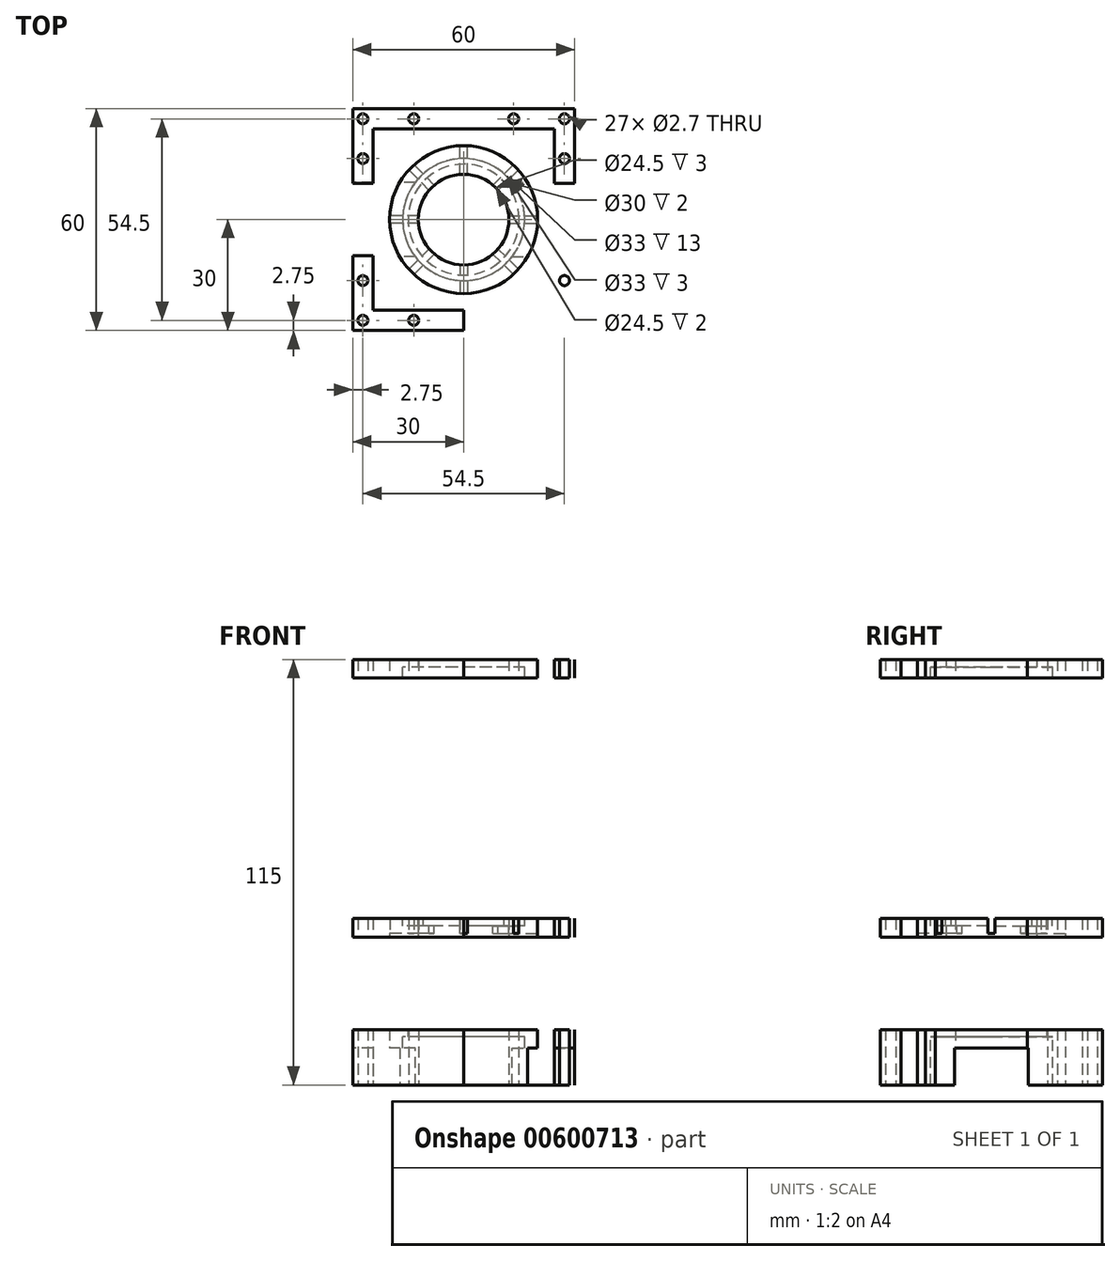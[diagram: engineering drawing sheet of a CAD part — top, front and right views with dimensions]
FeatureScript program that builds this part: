
annotation { "Feature Type Name" : "Feature", "Feature Type Description" : "" }
export const myFeature = defineFeature(function(context is Context, id is Id, definition is map)
    precondition{}
    {
        {
            var Q0;
            Q0=qCreatedBy(makeId("Top.planeOp"),FACE);
            var sketch = newSketch(context, id + "F0", { "sketchPlane" : qUnion([Q0])});
            skLineSegment(sketch, "E0.bottom", {"start": v(12.25, 0) * mm, "end": v(24.5, 0) * mm});
            skLineSegment(sketch, "E0.top", {"start": v(0, 24.5) * mm, "end": v(24.5, 24.5) * mm});
            skLineSegment(sketch, "E0.left", {"start": v(0, 12.25) * mm, "end": v(0, 24.5) * mm});
            skLineSegment(sketch, "E0.right", {"start": v(24.5, 0) * mm, "end": v(24.5, 24.5) * mm});
            skLineSegment(sketch, "E1", {"start": v(0, 24.5) * mm, "end": v(0, 30) * mm});
            skLineSegment(sketch, "E2", {"start": v(0, 30) * mm, "end": v(30, 30) * mm});
            skLineSegment(sketch, "E3", {"start": v(30, 30) * mm, "end": v(30, 9.75) * mm});
            skLineSegment(sketch, "E4", {"start": v(30, 9.75) * mm, "end": v(24.5, 9.75) * mm});
            skCircle(sketch, "E5", {"center": v(0, 0) * mm, "radius": 12.25 * mm});
            skLineSegment(sketch, "E6", {"start": v(0, 27.25) * mm, "end": v(38.5, 27.25) * mm, "construction": true});
            skLineSegment(sketch, "E7", {"start": v(27.25, 9.75) * mm, "end": v(27.25, 36.61) * mm, "construction": true});
            skCircle(sketch, "E8", {"center": v(27.25, 27.25) * mm, "radius": 1.35 * mm});
            skCircle(sketch, "E9", {"center": v(27.25, 16.5) * mm, "radius": 1.35 * mm});
            skCircle(sketch, "E10", {"center": v(13.5, 27.25) * mm, "radius": 1.35 * mm});
            skLineSegment(sketch, "E11.MirrorCS", {"start": v(-30, 30) * mm, "end": v(-30, 9.75) * mm});
            skLineSegment(sketch, "E12.MirrorCS", {"start": v(-24.5, 0) * mm, "end": v(-24.5, 24.5) * mm});
            skLineSegment(sketch, "E13.MirrorCS", {"start": v(-30, 9.75) * mm, "end": v(-24.5, 9.75) * mm});
            skCircle(sketch, "E14.MirrorC", {"center": v(-27.25, 16.5) * mm, "radius": 1.35 * mm});
            skCircle(sketch, "E15.MirrorC", {"center": v(-27.25, 27.25) * mm, "radius": 1.35 * mm});
            skCircle(sketch, "E16.MirrorC", {"center": v(-13.5, 27.25) * mm, "radius": 1.35 * mm});
            skLineSegment(sketch, "E17.MirrorCS", {"start": v(0, 30) * mm, "end": v(-30, 30) * mm});
            skLineSegment(sketch, "E18.MirrorCS", {"start": v(0, 24.5) * mm, "end": v(-24.5, 24.5) * mm});
            skLineSegment(sketch, "E19.MirrorCS", {"start": v(-30, -9.75) * mm, "end": v(-24.5, -9.75) * mm});
            skCircle(sketch, "E20.MirrorC", {"center": v(-27.25, -27.25) * mm, "radius": 1.35 * mm});
            skLineSegment(sketch, "E21.MirrorCS", {"start": v(0, -30) * mm, "end": v(-30, -30) * mm});
            skLineSegment(sketch, "E22.MirrorCS", {"start": v(0, -24.5) * mm, "end": v(-24.5, -24.5) * mm});
            skCircle(sketch, "E23.MirrorC", {"center": v(27.25, -16.5) * mm, "radius": 1.35 * mm});
            skCircle(sketch, "E24.MirrorC", {"center": v(-13.5, -27.25) * mm, "radius": 1.35 * mm});
            skCircle(sketch, "E25.MirrorC", {"center": v(27.25, -27.25) * mm, "radius": 1.35 * mm});
            skLineSegment(sketch, "E26.MirrorCS", {"start": v(30, -9.75) * mm, "end": v(24.5, -9.75) * mm});
            skCircle(sketch, "E27.MirrorC", {"center": v(-27.25, -16.5) * mm, "radius": 1.35 * mm});
            skCircle(sketch, "E28.MirrorC", {"center": v(13.5, -27.25) * mm, "radius": 1.35 * mm});
            skLineSegment(sketch, "E29.MirrorCS", {"start": v(-30, -30) * mm, "end": v(-30, -9.75) * mm});
            skLineSegment(sketch, "E30.MirrorCS", {"start": v(-24.5, 0) * mm, "end": v(-24.5, -24.5) * mm});
            skLineSegment(sketch, "E31.MirrorCS", {"start": v(30, -30) * mm, "end": v(30, -9.75) * mm});
            skLineSegment(sketch, "E32.MirrorCS", {"start": v(0, -30) * mm, "end": v(30, -30) * mm});
            skLineSegment(sketch, "E33.MirrorCS", {"start": v(0, -24.5) * mm, "end": v(24.5, -24.5) * mm});
            skLineSegment(sketch, "E34.MirrorCS", {"start": v(0, -24.5) * mm, "end": v(0, -30) * mm});
            skLineSegment(sketch, "E35.MirrorCS", {"start": v(24.5, 0) * mm, "end": v(24.5, -24.5) * mm});
            skCircle(sketch, "E36", {"center": v(0, 0) * mm, "radius": 20 * mm});
            skSolve(sketch);
        }
        {
            var Q0;
            Q0=qCreatedBy(makeId("Top.planeOp"),FACE);
            var sketch = newSketch(context, id + "F1", { "sketchPlane" : qUnion([Q0])});
            skCircle(sketch, "E37", {"center": v(0, 0) * mm, "radius": 45 * mm});
            skSolve(sketch);
        }
        {
            var Q0;
            Q0=makeQuery(id+"F1.imprint","IMPRINT",FACE,{"disambiguationData":[TD([[makeQuery(id+"F1.imprint","IMPRINT",EDGE,{"derivedFrom":sQuery(id+"F1.wireOp",EDGE,"E37")}),1.0]])]});
            extrude(context, id + "F2", {"entities" : qUnion([Q0]), "depth" : 5 * mm, "offsetDistance" : 25 * mm, "hasSecondDirection" : true, "secondDirectionOppositeDirection" : true, "secondDirectionDepth" : 5 * mm});
        }
        {
            var Q0;
            {var subQ1=sQuery(id+"F0.wireOp",EDGE,"E0.top");Q0=makeQuery(id+"F0.imprint","IMPRINT",FACE,{"disambiguationData":[TD([[makeQuery(id+"F0.imprint","IMPRINT",EDGE,{"derivedFrom":subQ1}),1.0]])]});}
            var Q1;
            {var subQ1=sQuery(id+"F0.wireOp",EDGE,"E0.bottom");Q1=makeQuery(id+"F0.imprint","IMPRINT",FACE,{"disambiguationData":[TD([[makeQuery(id+"F0.imprint","IMPRINT",EDGE,{"derivedFrom":subQ1}),1.0]])]});}
            var Q2;
            {var subQ7=sQuery(id+"F0.wireOp",EDGE,"E0.bottom");Q2=makeQuery(id+"F0.imprint","IMPRINT",FACE,{"disambiguationData":[TD([[makeQuery(id+"F0.imprint","IMPRINT",EDGE,{"derivedFrom":subQ7}),-1.0]])]});}
            var Q3;
            Q3=makeQuery(id+"F0.imprint","IMPRINT",FACE,{"disambiguationData":[TD([[makeQuery(id+"F0.imprint","IMPRINT",EDGE,{"derivedFrom":sQuery(id+"F0.wireOp",EDGE,"E23.MirrorC")}),1.0]])]});
            var Q4;
            {var subQ2=sQuery(id+"F0.wireOp",EDGE,"E19.MirrorCS");Q4=makeQuery(id+"F0.imprint","IMPRINT",FACE,{"disambiguationData":[TD([[makeQuery(id+"F0.imprint","IMPRINT",EDGE,{"derivedFrom":subQ2}),-1.0]])]});}
            var Q5;
            Q5=makeQuery(id+"F0.imprint","IMPRINT",FACE,{"disambiguationData":[TD([[makeQuery(id+"F0.imprint","IMPRINT",EDGE,{"derivedFrom":sQuery(id+"F0.wireOp",EDGE,"E1")}),1.0]])]});
            var Q6;
            Q6=makeQuery(id+"F2.opExtrude","SWEPT_BODY",BODY,{"disambiguationData":[OSD([sQuery(id+"F1.wireOp",EDGE,"E37")])]});
            extrude(context, id + "F3", {"entities" : qUnion([Q0, Q1, Q2, Q3, Q4, Q5]), "operationType" : NewBodyOperationType.REMOVE, "endBound" : BoundingType.UP_TO_BODY, "oppositeDirection" : true, "depth" : 25 * mm, "endBoundEntityBody" : qUnion([Q6]), "offsetDistance" : 25 * mm});
        }
        {
            var Q0;
            Q0=qCreatedBy(makeId("Top.planeOp"),FACE);
            cPlane(context, id + "F4", {"entities" : qUnion([Q0]), "cplaneType" : CPlaneType.OFFSET, "offset" : 25 * mm, "oppositeDirection" : true, "width" : 150 * mm, "height" : 150 * mm});
        }
        {
            var Q0;
            Q0=qCreatedBy(id+"F4.planeOp",FACE);
            var sketch = newSketch(context, id + "F5", { "sketchPlane" : qUnion([Q0])});
            skCircle(sketch, "E38", {"center": v(0, 0) * mm, "radius": 16.5 * mm});
            skLineSegment(sketch, "E39.bottom", {"start": v(-13.12, -10) * mm, "end": v(-43.87, -10) * mm});
            skLineSegment(sketch, "E39.top", {"start": v(-13.12, 10) * mm, "end": v(-43.87, 10) * mm});
            skCircle(sketch, "E40", {"center": v(0, 0) * mm, "radius": 15 * mm});
            skCircle(sketch, "E41", {"center": v(0, 0) * mm, "radius": 45 * mm});
            skLineSegment(sketch, "E42.MirrorCS", {"start": v(13.12, 10) * mm, "end": v(43.87, 10) * mm});
            skLineSegment(sketch, "E43.MirrorCS", {"start": v(13.12, -10) * mm, "end": v(43.87, -10) * mm});
            skSolve(sketch);
        }
        {
            var Q0;
            Q0=makeQuery(id+"F5.imprint","IMPRINT",FACE,{"disambiguationData":[TD([[makeQuery(id+"F5.imprint","IMPRINT",EDGE,{"derivedFrom":sQuery(id+"F5.wireOp",EDGE,"E40")}),-1.0]])]});
            extrude(context, id + "F6", {"entities" : qUnion([Q0]), "oppositeDirection" : true, "depth" : 2 * mm, "offsetDistance" : 25 * mm});
        }
        {
            var Q0;
            {var subQ0=sQuery(id+"F5.wireOp",EDGE,"E42.MirrorCS");Q0=makeQuery(id+"F5.imprint","IMPRINT",FACE,{"disambiguationData":[TD([[makeQuery(id+"F5.imprint","IMPRINT",EDGE,{"derivedFrom":subQ0}),-1.0]])]});}
            var Q1;
            {var subQ0=sQuery(id+"F5.wireOp",EDGE,"E39.bottom");Q1=makeQuery(id+"F5.imprint","IMPRINT",FACE,{"disambiguationData":[TD([[makeQuery(id+"F5.imprint","IMPRINT",EDGE,{"derivedFrom":subQ0}),-1.0]])]});}
            extrude(context, id + "F7", {"entities" : qUnion([Q0, Q1]), "operationType" : NewBodyOperationType.ADD, "oppositeDirection" : true, "depth" : 5 * mm, "offsetDistance" : 25 * mm});
        }
        {
            var Q0;
            {var subQ0=sQuery(id+"F5.wireOp",EDGE,"E39.top");Q0=makeQuery(id+"F5.imprint","IMPRINT",FACE,{"disambiguationData":[TD([[makeQuery(id+"F5.imprint","IMPRINT",EDGE,{"derivedFrom":subQ0}),-1.0]])]});}
            var Q1;
            {var subQ0=sQuery(id+"F5.wireOp",EDGE,"E39.bottom");Q1=makeQuery(id+"F5.imprint","IMPRINT",FACE,{"disambiguationData":[TD([[makeQuery(id+"F5.imprint","IMPRINT",EDGE,{"derivedFrom":subQ0}),1.0]])]});}
            extrude(context, id + "F8", {"entities" : qUnion([Q0, Q1]), "operationType" : NewBodyOperationType.ADD, "oppositeDirection" : true, "depth" : 15 * mm, "offsetDistance" : 25 * mm});
        }
        {
            var Q0;
            Q0=qCreatedBy(makeId("Top.planeOp"),FACE);
            cPlane(context, id + "F9", {"entities" : qUnion([Q0]), "cplaneType" : CPlaneType.OFFSET, "offset" : 75 * mm, "width" : 150 * mm, "height" : 150 * mm});
        }
        {
            var Q0;
            Q0=qCreatedBy(id+"F9.planeOp",FACE);
            var sketch = newSketch(context, id + "F10", { "sketchPlane" : qUnion([Q0])});
            skCircle(sketch, "E44", {"center": v(0, 0) * mm, "radius": 45 * mm});
            skCircle(sketch, "E45", {"center": v(0, 0) * mm, "radius": 5 * mm});
            skCircle(sketch, "E46", {"center": v(0, 0) * mm, "radius": 16.5 * mm});
            skSolve(sketch);
        }
        {
            var Q0;
            Q0=makeQuery(id+"F10.imprint","IMPRINT",FACE,{"disambiguationData":[TD([[makeQuery(id+"F10.imprint","IMPRINT",EDGE,{"derivedFrom":sQuery(id+"F10.wireOp",EDGE,"E44")}),1.0]])]});
            extrude(context, id + "F11", {"entities" : qUnion([Q0]), "oppositeDirection" : true, "depth" : 5 * mm, "offsetDistance" : 25 * mm});
        }
        {
            var Q0;
            Q0=makeQuery(id+"F10.imprint","IMPRINT",FACE,{"disambiguationData":[TD([[makeQuery(id+"F10.imprint","IMPRINT",EDGE,{"derivedFrom":sQuery(id+"F10.wireOp",EDGE,"JAyOYwTu-o1NB-EITc-PAzT-4Qr8e6rMUSNN.bottom")}),-1.0]])]});
            var Q1;
            Q1=makeQuery(id+"F10.imprint","IMPRINT",FACE,{"disambiguationData":[TD([[makeQuery(id+"F10.imprint","IMPRINT",EDGE,{"derivedFrom":sQuery(id+"F10.wireOp",EDGE,"E45")}),-1.0]])]});
            extrude(context, id + "F12", {"entities" : qUnion([Q0, Q1]), "operationType" : NewBodyOperationType.ADD, "oppositeDirection" : true, "depth" : 2 * mm, "offsetDistance" : 25 * mm});
        }
        {
            var Q0;
            Q0=makeQuery(id+"F2.opExtrude","CAP_FACE",FACE,{"disambiguationData":[OSD([sQuery(id+"F1.wireOp",EDGE,"E37")])],"isStart":false});
            var sketch = newSketch(context, id + "F13", { "sketchPlane" : qUnion([Q0])});
            skCircle(sketch, "E47", {"center": v(0, 0) * mm, "radius": 16.5 * mm});
            skLineSegment(sketch, "E48.bottom", {"start": v(1, 12.2) * mm, "end": v(-1, 12.2) * mm});
            skLineSegment(sketch, "E48.top", {"start": v(1, 20.8) * mm, "end": v(-1, 20.8) * mm});
            skLineSegment(sketch, "E48.left", {"start": v(1, 12.2) * mm, "end": v(1, 20.8) * mm});
            skLineSegment(sketch, "E48.right", {"start": v(-1, 12.2) * mm, "end": v(-1, 20.8) * mm});
            skPoint(sketch, "E48.middle", {"position": v(0, 16.5) * mm});
            skLineSegment(sketch, "E49.1.0", {"start": v(-9.34, 7.93) * mm, "end": v(-15.4, 14) * mm});
            skLineSegment(sketch, "E49.1.1", {"start": v(-7.93, 9.34) * mm, "end": v(-9.34, 7.93) * mm});
            skLineSegment(sketch, "E49.1.2", {"start": v(-7.93, 9.34) * mm, "end": v(-14, 15.4) * mm});
            skLineSegment(sketch, "E49.1.3", {"start": v(-14, 15.4) * mm, "end": v(-15.4, 14) * mm});
            skLineSegment(sketch, "E49.2.0", {"start": v(-12.2, -1) * mm, "end": v(-20.8, -1) * mm});
            skLineSegment(sketch, "E49.2.1", {"start": v(-12.2, 1) * mm, "end": v(-12.2, -1) * mm});
            skLineSegment(sketch, "E49.2.2", {"start": v(-12.2, 1) * mm, "end": v(-20.8, 1) * mm});
            skLineSegment(sketch, "E49.2.3", {"start": v(-20.8, 1) * mm, "end": v(-20.8, -1) * mm});
            skLineSegment(sketch, "E49.3.0", {"start": v(-7.93, -9.34) * mm, "end": v(-14, -15.4) * mm});
            skLineSegment(sketch, "E49.3.1", {"start": v(-9.34, -7.93) * mm, "end": v(-7.93, -9.34) * mm});
            skLineSegment(sketch, "E49.3.2", {"start": v(-9.34, -7.93) * mm, "end": v(-15.4, -14) * mm});
            skLineSegment(sketch, "E49.3.3", {"start": v(-15.4, -14) * mm, "end": v(-14, -15.4) * mm});
            skLineSegment(sketch, "E49.4.0", {"start": v(1, -12.2) * mm, "end": v(1, -20.8) * mm});
            skLineSegment(sketch, "E49.4.1", {"start": v(-1, -12.2) * mm, "end": v(1, -12.2) * mm});
            skLineSegment(sketch, "E49.4.2", {"start": v(-1, -12.2) * mm, "end": v(-1, -20.8) * mm});
            skLineSegment(sketch, "E49.4.3", {"start": v(-1, -20.8) * mm, "end": v(1, -20.8) * mm});
            skLineSegment(sketch, "E49.5.0", {"start": v(9.34, -7.93) * mm, "end": v(15.4, -14) * mm});
            skLineSegment(sketch, "E49.5.1", {"start": v(7.93, -9.34) * mm, "end": v(9.34, -7.93) * mm});
            skLineSegment(sketch, "E49.5.2", {"start": v(7.93, -9.34) * mm, "end": v(14, -15.4) * mm});
            skLineSegment(sketch, "E49.5.3", {"start": v(14, -15.4) * mm, "end": v(15.4, -14) * mm});
            skLineSegment(sketch, "E49.6.0", {"start": v(12.2, 1) * mm, "end": v(20.8, 1) * mm});
            skLineSegment(sketch, "E49.6.1", {"start": v(12.2, -1) * mm, "end": v(12.2, 1) * mm});
            skLineSegment(sketch, "E49.6.2", {"start": v(12.2, -1) * mm, "end": v(20.8, -1) * mm});
            skLineSegment(sketch, "E49.6.3", {"start": v(20.8, -1) * mm, "end": v(20.8, 1) * mm});
            skLineSegment(sketch, "E49.7.0", {"start": v(7.93, 9.34) * mm, "end": v(14, 15.4) * mm});
            skLineSegment(sketch, "E49.7.1", {"start": v(9.34, 7.93) * mm, "end": v(7.93, 9.34) * mm});
            skLineSegment(sketch, "E49.7.2", {"start": v(9.34, 7.93) * mm, "end": v(15.4, 14) * mm});
            skLineSegment(sketch, "E49.7.3", {"start": v(15.4, 14) * mm, "end": v(14, 15.4) * mm});
            skSolve(sketch);
        }
        {
            var Q0;
            {var subQ0=sQuery(id+"F13.wireOp",EDGE,"E48.left");var subQ1=sQuery(id+"F13.wireOp",EDGE,"E47");var subQ2=makeQuery(id+"F13.imprint","INTERSECT",VERTEX,{"derivedFrom":[subQ1,subQ0]});Q0=makeQuery(id+"F13.imprint","IMPRINT",FACE,{"disambiguationData":[TD([[makeQuery(id+"F13.imprint","IMPRINT",EDGE,{"disambiguationData":[TD([[subQ2,-1.0]])],"derivedFrom":subQ1}),1.0]])]});}
            var Q1;
            {var subQ5=sQuery(id+"F13.wireOp",EDGE,"E48.top");Q1=makeQuery(id+"F13.imprint","IMPRINT",FACE,{"disambiguationData":[TD([[makeQuery(id+"F13.imprint","IMPRINT",EDGE,{"derivedFrom":subQ5}),1.0]])]});}
            var Q2;
            {var subQ5=sQuery(id+"F13.wireOp",EDGE,"E49.7.3");Q2=makeQuery(id+"F13.imprint","IMPRINT",FACE,{"disambiguationData":[TD([[makeQuery(id+"F13.imprint","IMPRINT",EDGE,{"derivedFrom":subQ5}),1.0]])]});}
            var Q3;
            {var subQ0=sQuery(id+"F13.wireOp",EDGE,"E49.7.2");var subQ1=sQuery(id+"F13.wireOp",EDGE,"E47");var subQ2=makeQuery(id+"F13.imprint","INTERSECT",VERTEX,{"derivedFrom":[subQ1,subQ0]});Q3=makeQuery(id+"F13.imprint","IMPRINT",FACE,{"disambiguationData":[TD([[makeQuery(id+"F13.imprint","IMPRINT",EDGE,{"disambiguationData":[TD([[subQ2,-1.0]])],"derivedFrom":subQ1}),1.0]])]});}
            var Q4;
            {var subQ5=sQuery(id+"F13.wireOp",EDGE,"E49.6.3");Q4=makeQuery(id+"F13.imprint","IMPRINT",FACE,{"disambiguationData":[TD([[makeQuery(id+"F13.imprint","IMPRINT",EDGE,{"derivedFrom":subQ5}),1.0]])]});}
            var Q5;
            {var subQ0=sQuery(id+"F13.wireOp",EDGE,"E49.6.0");var subQ1=sQuery(id+"F13.wireOp",EDGE,"E47");var subQ2=makeQuery(id+"F13.imprint","INTERSECT",VERTEX,{"derivedFrom":[subQ1,subQ0]});Q5=makeQuery(id+"F13.imprint","IMPRINT",FACE,{"disambiguationData":[TD([[makeQuery(id+"F13.imprint","IMPRINT",EDGE,{"disambiguationData":[TD([[subQ2,1.0]])],"derivedFrom":subQ1}),1.0]])]});}
            var Q6;
            {var subQ5=sQuery(id+"F13.wireOp",EDGE,"E49.5.3");Q6=makeQuery(id+"F13.imprint","IMPRINT",FACE,{"disambiguationData":[TD([[makeQuery(id+"F13.imprint","IMPRINT",EDGE,{"derivedFrom":subQ5}),1.0]])]});}
            var Q7;
            {var subQ0=sQuery(id+"F13.wireOp",EDGE,"E49.5.2");var subQ1=sQuery(id+"F13.wireOp",EDGE,"E47");var subQ2=makeQuery(id+"F13.imprint","INTERSECT",VERTEX,{"derivedFrom":[subQ1,subQ0]});Q7=makeQuery(id+"F13.imprint","IMPRINT",FACE,{"disambiguationData":[TD([[makeQuery(id+"F13.imprint","IMPRINT",EDGE,{"disambiguationData":[TD([[subQ2,-1.0]])],"derivedFrom":subQ1}),1.0]])]});}
            var Q8;
            {var subQ5=sQuery(id+"F13.wireOp",EDGE,"E49.4.3");Q8=makeQuery(id+"F13.imprint","IMPRINT",FACE,{"disambiguationData":[TD([[makeQuery(id+"F13.imprint","IMPRINT",EDGE,{"derivedFrom":subQ5}),1.0]])]});}
            var Q9;
            {var subQ0=sQuery(id+"F13.wireOp",EDGE,"E49.4.2");var subQ1=sQuery(id+"F13.wireOp",EDGE,"E47");var subQ2=makeQuery(id+"F13.imprint","INTERSECT",VERTEX,{"derivedFrom":[subQ1,subQ0]});Q9=makeQuery(id+"F13.imprint","IMPRINT",FACE,{"disambiguationData":[TD([[makeQuery(id+"F13.imprint","IMPRINT",EDGE,{"disambiguationData":[TD([[subQ2,-1.0]])],"derivedFrom":subQ1}),1.0]])]});}
            var Q10;
            {var subQ5=sQuery(id+"F13.wireOp",EDGE,"E49.3.3");Q10=makeQuery(id+"F13.imprint","IMPRINT",FACE,{"disambiguationData":[TD([[makeQuery(id+"F13.imprint","IMPRINT",EDGE,{"derivedFrom":subQ5}),1.0]])]});}
            var Q11;
            {var subQ0=sQuery(id+"F13.wireOp",EDGE,"E49.3.2");var subQ1=sQuery(id+"F13.wireOp",EDGE,"E47");var subQ2=makeQuery(id+"F13.imprint","INTERSECT",VERTEX,{"derivedFrom":[subQ1,subQ0]});Q11=makeQuery(id+"F13.imprint","IMPRINT",FACE,{"disambiguationData":[TD([[makeQuery(id+"F13.imprint","IMPRINT",EDGE,{"disambiguationData":[TD([[subQ2,-1.0]])],"derivedFrom":subQ1}),1.0]])]});}
            var Q12;
            {var subQ5=sQuery(id+"F13.wireOp",EDGE,"E49.2.3");Q12=makeQuery(id+"F13.imprint","IMPRINT",FACE,{"disambiguationData":[TD([[makeQuery(id+"F13.imprint","IMPRINT",EDGE,{"derivedFrom":subQ5}),1.0]])]});}
            var Q13;
            {var subQ0=sQuery(id+"F13.wireOp",EDGE,"E49.2.2");var subQ1=sQuery(id+"F13.wireOp",EDGE,"E47");var subQ2=makeQuery(id+"F13.imprint","INTERSECT",VERTEX,{"derivedFrom":[subQ1,subQ0]});Q13=makeQuery(id+"F13.imprint","IMPRINT",FACE,{"disambiguationData":[TD([[makeQuery(id+"F13.imprint","IMPRINT",EDGE,{"disambiguationData":[TD([[subQ2,-1.0]])],"derivedFrom":subQ1}),1.0]])]});}
            var Q14;
            {var subQ5=sQuery(id+"F13.wireOp",EDGE,"E49.1.3");Q14=makeQuery(id+"F13.imprint","IMPRINT",FACE,{"disambiguationData":[TD([[makeQuery(id+"F13.imprint","IMPRINT",EDGE,{"derivedFrom":subQ5}),1.0]])]});}
            var Q15;
            {var subQ0=sQuery(id+"F13.wireOp",EDGE,"E49.1.2");var subQ1=sQuery(id+"F13.wireOp",EDGE,"E47");var subQ2=makeQuery(id+"F13.imprint","INTERSECT",VERTEX,{"derivedFrom":[subQ1,subQ0]});Q15=makeQuery(id+"F13.imprint","IMPRINT",FACE,{"disambiguationData":[TD([[makeQuery(id+"F13.imprint","IMPRINT",EDGE,{"disambiguationData":[TD([[subQ2,-1.0]])],"derivedFrom":subQ1}),1.0]])]});}
            extrude(context, id + "F14", {"entities" : qUnion([Q0, Q1, Q2, Q3, Q4, Q5, Q6, Q7, Q8, Q9, Q10, Q11, Q12, Q13, Q14, Q15]), "operationType" : NewBodyOperationType.REMOVE, "oppositeDirection" : true, "depth" : 4 * mm, "offsetDistance" : 25 * mm});
        }
        {
            var Q0;
            {var subQ0=sQuery(id+"F13.wireOp",EDGE,"E49.3.0");var subQ1=sQuery(id+"F13.wireOp",EDGE,"E47");var subQ2=makeQuery(id+"F13.imprint","INTERSECT",VERTEX,{"derivedFrom":[subQ1,subQ0]});Q0=makeQuery(id+"F13.imprint","IMPRINT",FACE,{"disambiguationData":[TD([[makeQuery(id+"F13.imprint","IMPRINT",EDGE,{"disambiguationData":[TD([[subQ2,-1.0]])],"derivedFrom":subQ1}),1.0]])]});}
            var Q1;
            {var subQ0=sQuery(id+"F13.wireOp",EDGE,"E49.2.0");var subQ1=sQuery(id+"F13.wireOp",EDGE,"E47");var subQ2=makeQuery(id+"F13.imprint","INTERSECT",VERTEX,{"derivedFrom":[subQ1,subQ0]});Q1=makeQuery(id+"F13.imprint","IMPRINT",FACE,{"disambiguationData":[TD([[makeQuery(id+"F13.imprint","IMPRINT",EDGE,{"disambiguationData":[TD([[subQ2,-1.0]])],"derivedFrom":subQ1}),1.0]])]});}
            var Q2;
            {var subQ0=sQuery(id+"F13.wireOp",EDGE,"E49.1.0");var subQ1=sQuery(id+"F13.wireOp",EDGE,"E47");var subQ2=makeQuery(id+"F13.imprint","INTERSECT",VERTEX,{"derivedFrom":[subQ1,subQ0]});Q2=makeQuery(id+"F13.imprint","IMPRINT",FACE,{"disambiguationData":[TD([[makeQuery(id+"F13.imprint","IMPRINT",EDGE,{"disambiguationData":[TD([[subQ2,-1.0]])],"derivedFrom":subQ1}),1.0]])]});}
            var Q3;
            {var subQ0=sQuery(id+"F13.wireOp",EDGE,"E49.4.0");var subQ1=sQuery(id+"F13.wireOp",EDGE,"E47");var subQ2=makeQuery(id+"F13.imprint","INTERSECT",VERTEX,{"derivedFrom":[subQ1,subQ0]});Q3=makeQuery(id+"F13.imprint","IMPRINT",FACE,{"disambiguationData":[TD([[makeQuery(id+"F13.imprint","IMPRINT",EDGE,{"disambiguationData":[TD([[subQ2,-1.0]])],"derivedFrom":subQ1}),1.0]])]});}
            var Q4;
            {var subQ0=sQuery(id+"F13.wireOp",EDGE,"E49.5.0");var subQ1=sQuery(id+"F13.wireOp",EDGE,"E47");var subQ2=makeQuery(id+"F13.imprint","INTERSECT",VERTEX,{"derivedFrom":[subQ1,subQ0]});Q4=makeQuery(id+"F13.imprint","IMPRINT",FACE,{"disambiguationData":[TD([[makeQuery(id+"F13.imprint","IMPRINT",EDGE,{"disambiguationData":[TD([[subQ2,-1.0]])],"derivedFrom":subQ1}),1.0]])]});}
            var Q5;
            {var subQ0=sQuery(id+"F13.wireOp",EDGE,"E49.7.2");var subQ1=sQuery(id+"F13.wireOp",EDGE,"E47");var subQ2=makeQuery(id+"F13.imprint","INTERSECT",VERTEX,{"derivedFrom":[subQ1,subQ0]});Q5=makeQuery(id+"F13.imprint","IMPRINT",FACE,{"disambiguationData":[TD([[makeQuery(id+"F13.imprint","IMPRINT",EDGE,{"disambiguationData":[TD([[subQ2,1.0]])],"derivedFrom":subQ1}),1.0]])]});}
            var Q6;
            {var subQ0=sQuery(id+"F13.wireOp",EDGE,"E49.7.0");var subQ1=sQuery(id+"F13.wireOp",EDGE,"E47");var subQ2=makeQuery(id+"F13.imprint","INTERSECT",VERTEX,{"derivedFrom":[subQ1,subQ0]});Q6=makeQuery(id+"F13.imprint","IMPRINT",FACE,{"disambiguationData":[TD([[makeQuery(id+"F13.imprint","IMPRINT",EDGE,{"disambiguationData":[TD([[subQ2,-1.0]])],"derivedFrom":subQ1}),1.0]])]});}
            var Q7;
            {var subQ0=sQuery(id+"F13.wireOp",EDGE,"E48.right");var subQ1=sQuery(id+"F13.wireOp",EDGE,"E47");var subQ2=makeQuery(id+"F13.imprint","INTERSECT",VERTEX,{"derivedFrom":[subQ1,subQ0]});Q7=makeQuery(id+"F13.imprint","IMPRINT",FACE,{"disambiguationData":[TD([[makeQuery(id+"F13.imprint","IMPRINT",EDGE,{"disambiguationData":[TD([[subQ2,-1.0]])],"derivedFrom":subQ1}),1.0]])]});}
            extrude(context, id + "F15", {"entities" : qUnion([Q0, Q1, Q2, Q3, Q4, Q5, Q6, Q7]), "operationType" : NewBodyOperationType.REMOVE, "oppositeDirection" : true, "depth" : 2 * mm, "offsetDistance" : 25 * mm});
        }
        {
            var Q0;
            Q0=makeQuery(id+"F11.opExtrude","CAP_FACE",FACE,{"disambiguationData":[OSD([sQuery(id+"F10.wireOp",EDGE,"E44"),sQuery(id+"F10.wireOp",EDGE,"E46")])],"isStart":false});
            var sketch = newSketch(context, id + "F16", { "sketchPlane" : qUnion([Q0])});
            skCircle(sketch, "E50", {"center": v(0, 0) * mm, "radius": 20 * mm});
            skCircle(sketch, "E51", {"center": v(0, 0) * mm, "radius": 22 * mm});
            skSolve(sketch);
        }
        {
            var Q0;
            Q0=makeQuery(id+"F16.imprint","IMPRINT",FACE,{"disambiguationData":[TD([[makeQuery(id+"F16.imprint","IMPRINT",EDGE,{"derivedFrom":sQuery(id+"F16.wireOp",EDGE,"E50")}),-1.0]])]});
            extrude(context, id + "F17", {"entities" : qUnion([Q0]), "operationType" : NewBodyOperationType.REMOVE, "oppositeDirection" : true, "depth" : 2 * mm, "offsetDistance" : 25 * mm});
        }
        {
            var Q0;
            Q0=makeQuery(id+"F17.boolean.opBoolean","COPY",EDGE,{"derivedFrom":makeQuery(id+"F17.opExtrude","CAP_EDGE",EDGE,{"disambiguationData":[OSD([sQuery(id+"F16.wireOp",EDGE,"E51")])],"isStart":false})});
            var Q1;
            Q1=makeQuery(id+"F17.boolean.opBoolean","COPY",EDGE,{"derivedFrom":makeQuery(id+"F17.opExtrude","CAP_EDGE",EDGE,{"disambiguationData":[OSD([sQuery(id+"F16.wireOp",EDGE,"E50")])],"isStart":false})});
            fillet(context, id + "F18", {"entities" : qUnion([Q0, Q1]), "radius" : 1 * mm, "tangentPropagation" : true, "allowEdgeOverflow" : false});
        }
        {
            var Q0;
            Q0=makeQuery(id+"F10.imprint","IMPRINT",FACE,{"disambiguationData":[TD([[makeQuery(id+"F10.imprint","IMPRINT",EDGE,{"derivedFrom":sQuery(id+"F10.wireOp",EDGE,"E45")}),1.0]])]});
            extrude(context, id + "F19", {"entities" : qUnion([Q0]), "oppositeDirection" : true, "depth" : 25 * mm, "offsetDistance" : 25 * mm});
        }
        {
            var Q0;
            Q0=makeQuery(id+"F3.boolean.opBoolean","SPLIT",FACE,{"disambiguationData":[TD([makeQuery(id+"F3.opExtrude","SWEPT_FACE",FACE,{"disambiguationData":[OSD([sQuery(id+"F0.wireOp",EDGE,"E8")])]})])],"derivedFrom":makeQuery(id+"F2.opExtrude","CAP_FACE",FACE,{"disambiguationData":[OSD([sQuery(id+"F1.wireOp",EDGE,"E37")])],"isStart":true})});
            var Q1;
            Q1=makeQuery(id+"F0.imprint","IMPRINT",FACE,{"disambiguationData":[TD([[makeQuery(id+"F0.imprint","IMPRINT",EDGE,{"derivedFrom":sQuery(id+"F0.wireOp",EDGE,"E10")}),1.0]])]});
            var Q2;
            Q2=makeQuery(id+"F3.boolean.opBoolean","SPLIT",FACE,{"disambiguationData":[TD([makeQuery(id+"F3.opExtrude","SWEPT_FACE",FACE,{"disambiguationData":[OSD([sQuery(id+"F0.wireOp",EDGE,"E16.MirrorC")])]})])],"derivedFrom":makeQuery(id+"F2.opExtrude","CAP_FACE",FACE,{"disambiguationData":[OSD([sQuery(id+"F1.wireOp",EDGE,"E37")])],"isStart":true})});
            var Q3;
            Q3=makeQuery(id+"F3.boolean.opBoolean","SPLIT",FACE,{"disambiguationData":[TD([makeQuery(id+"F3.opExtrude","SWEPT_FACE",FACE,{"disambiguationData":[OSD([sQuery(id+"F0.wireOp",EDGE,"E15.MirrorC")])]})])],"derivedFrom":makeQuery(id+"F2.opExtrude","CAP_FACE",FACE,{"disambiguationData":[OSD([sQuery(id+"F1.wireOp",EDGE,"E37")])],"isStart":true})});
            var Q4;
            Q4=makeQuery(id+"F3.boolean.opBoolean","SPLIT",FACE,{"disambiguationData":[TD([makeQuery(id+"F3.opExtrude","SWEPT_FACE",FACE,{"disambiguationData":[OSD([sQuery(id+"F0.wireOp",EDGE,"E14.MirrorC")])]})])],"derivedFrom":makeQuery(id+"F2.opExtrude","CAP_FACE",FACE,{"disambiguationData":[OSD([sQuery(id+"F1.wireOp",EDGE,"E37")])],"isStart":true})});
            var Q5;
            Q5=makeQuery(id+"F3.boolean.opBoolean","SPLIT",FACE,{"disambiguationData":[TD([makeQuery(id+"F3.opExtrude","SWEPT_FACE",FACE,{"disambiguationData":[OSD([sQuery(id+"F0.wireOp",EDGE,"E27.MirrorC")])]})])],"derivedFrom":makeQuery(id+"F2.opExtrude","CAP_FACE",FACE,{"disambiguationData":[OSD([sQuery(id+"F1.wireOp",EDGE,"E37")])],"isStart":true})});
            var Q6;
            Q6=makeQuery(id+"F3.boolean.opBoolean","SPLIT",FACE,{"disambiguationData":[TD([makeQuery(id+"F3.opExtrude","SWEPT_FACE",FACE,{"disambiguationData":[OSD([sQuery(id+"F0.wireOp",EDGE,"E20.MirrorC")])]})])],"derivedFrom":makeQuery(id+"F2.opExtrude","CAP_FACE",FACE,{"disambiguationData":[OSD([sQuery(id+"F1.wireOp",EDGE,"E37")])],"isStart":true})});
            var Q7;
            Q7=makeQuery(id+"F3.boolean.opBoolean","SPLIT",FACE,{"disambiguationData":[TD([makeQuery(id+"F3.opExtrude","SWEPT_FACE",FACE,{"disambiguationData":[OSD([sQuery(id+"F0.wireOp",EDGE,"E24.MirrorC")])]})])],"derivedFrom":makeQuery(id+"F2.opExtrude","CAP_FACE",FACE,{"disambiguationData":[OSD([sQuery(id+"F1.wireOp",EDGE,"E37")])],"isStart":true})});
            var Q8;
            Q8=makeQuery(id+"F3.boolean.opBoolean","SPLIT",FACE,{"disambiguationData":[TD([makeQuery(id+"F3.opExtrude","SWEPT_FACE",FACE,{"disambiguationData":[OSD([sQuery(id+"F0.wireOp",EDGE,"E28.MirrorC")])]})])],"derivedFrom":makeQuery(id+"F2.opExtrude","CAP_FACE",FACE,{"disambiguationData":[OSD([sQuery(id+"F1.wireOp",EDGE,"E37")])],"isStart":true})});
            var Q9;
            Q9=makeQuery(id+"F3.boolean.opBoolean","SPLIT",FACE,{"disambiguationData":[TD([makeQuery(id+"F3.opExtrude","SWEPT_FACE",FACE,{"disambiguationData":[OSD([sQuery(id+"F0.wireOp",EDGE,"E25.MirrorC")])]})])],"derivedFrom":makeQuery(id+"F2.opExtrude","CAP_FACE",FACE,{"disambiguationData":[OSD([sQuery(id+"F1.wireOp",EDGE,"E37")])],"isStart":true})});
            var Q10;
            Q10=makeQuery(id+"F3.boolean.opBoolean","SPLIT",FACE,{"disambiguationData":[TD([makeQuery(id+"F3.opExtrude","SWEPT_FACE",FACE,{"disambiguationData":[OSD([sQuery(id+"F0.wireOp",EDGE,"E23.MirrorC")])]})])],"derivedFrom":makeQuery(id+"F2.opExtrude","CAP_FACE",FACE,{"disambiguationData":[OSD([sQuery(id+"F1.wireOp",EDGE,"E37")])],"isStart":true})});
            var Q11;
            Q11=makeQuery(id+"F3.boolean.opBoolean","SPLIT",FACE,{"disambiguationData":[TD([makeQuery(id+"F3.opExtrude","SWEPT_FACE",FACE,{"disambiguationData":[OSD([sQuery(id+"F0.wireOp",EDGE,"E9")])]})])],"derivedFrom":makeQuery(id+"F2.opExtrude","CAP_FACE",FACE,{"disambiguationData":[OSD([sQuery(id+"F1.wireOp",EDGE,"E37")])],"isStart":true})});
            extrude(context, id + "F20", {"entities" : qUnion([Q0, Q1, Q2, Q3, Q4, Q5, Q6, Q7, Q8, Q9, Q10, Q11]), "operationType" : NewBodyOperationType.REMOVE, "endBound" : BoundingType.THROUGH_ALL, "oppositeDirection" : true, "depth" : 25 * mm, "offsetDistance" : 25 * mm, "hasSecondDirection" : true, "secondDirectionBound" : BoundingType.THROUGH_ALL, "secondDirectionOppositeDirection" : false, "secondDirectionDepth" : 25 * mm});
        }
        {
            var Q0;
            Q0=makeQuery(id+"F3.boolean.opBoolean","SPLIT",FACE,{"disambiguationData":[TD([makeQuery(id+"F3.opExtrude","SWEPT_FACE",FACE,{"disambiguationData":[OSD([sQuery(id+"F0.wireOp",EDGE,"E5")])]})])],"derivedFrom":makeQuery(id+"F2.opExtrude","CAP_FACE",FACE,{"disambiguationData":[OSD([sQuery(id+"F1.wireOp",EDGE,"E37")])],"isStart":true})});
            extrude(context, id + "F21", {"entities" : qUnion([Q0]), "operationType" : NewBodyOperationType.REMOVE, "endBound" : BoundingType.THROUGH_ALL, "oppositeDirection" : true, "depth" : 25 * mm, "offsetDistance" : 25 * mm});
        }
    });
